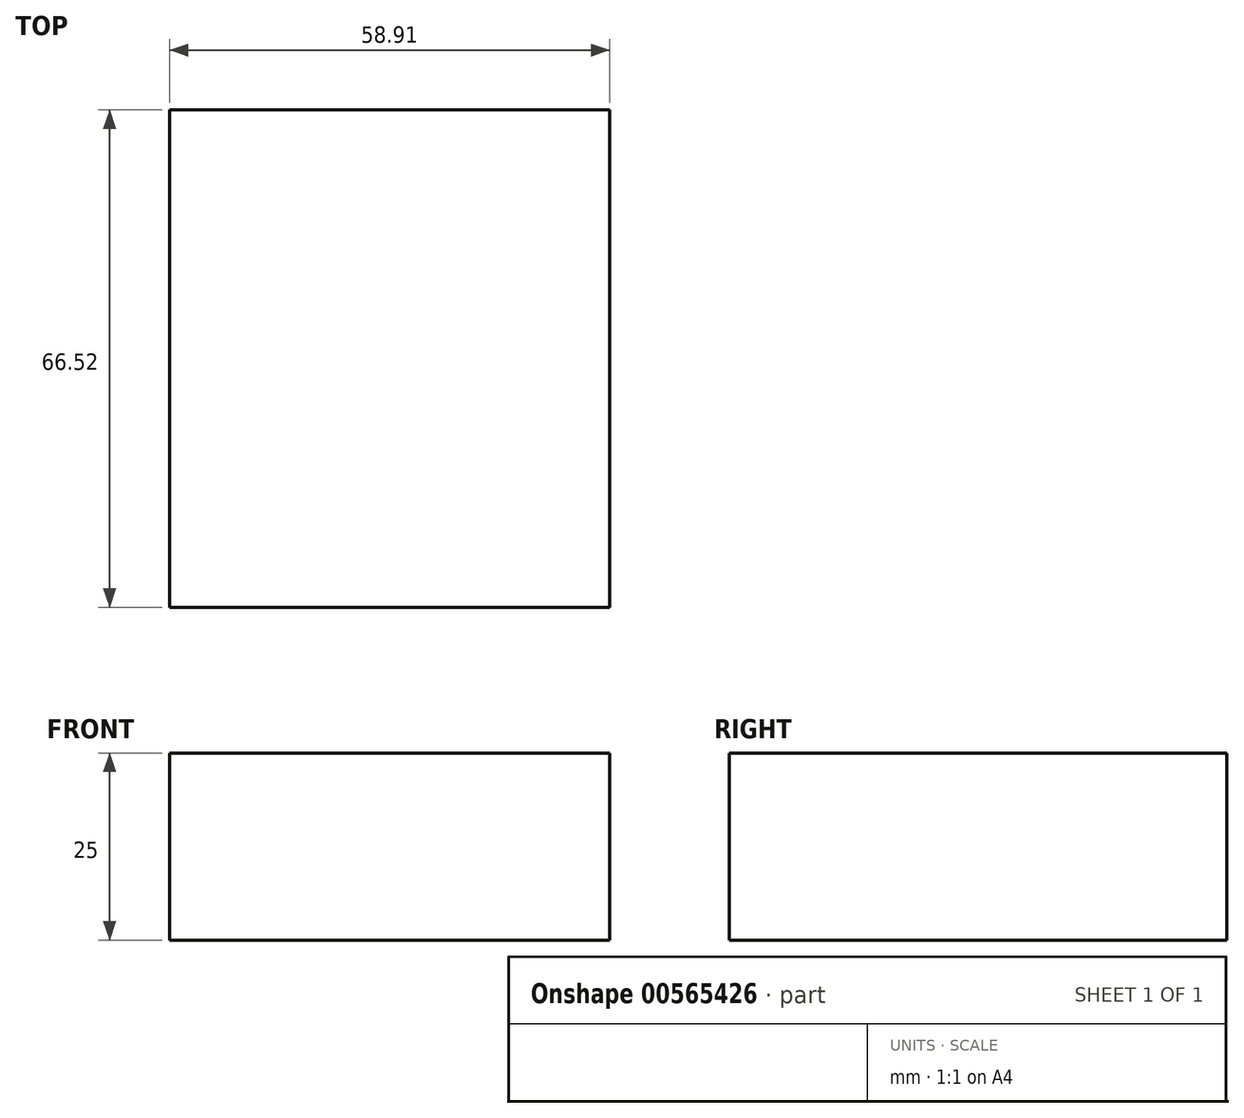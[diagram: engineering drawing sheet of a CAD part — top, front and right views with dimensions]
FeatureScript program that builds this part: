
annotation { "Feature Type Name" : "Feature", "Feature Type Description" : "" }
export const myFeature = defineFeature(function(context is Context, id is Id, definition is map)
    precondition{}
    {
        {
            var Q0;
            Q0=qCreatedBy(makeId("Top.planeOp"),FACE);
            var sketch = newSketch(context, id + "F0", { "sketchPlane" : qUnion([Q0])});
            skLineSegment(sketch, "E0", {"start": v(0, 0) * mm, "end": v(58.91, 0) * mm});
            skLineSegment(sketch, "E1", {"start": v(58.91, 0) * mm, "end": v(58.91, 66.52) * mm});
            skLineSegment(sketch, "E2", {"start": v(58.91, 66.52) * mm, "end": v(0, 66.52) * mm});
            skLineSegment(sketch, "E3", {"start": v(0, 66.52) * mm, "end": v(0, 0) * mm});
            skSolve(sketch);
        }
        {
            var Q0;
            Q0=makeQuery(id+"F0.imprint","IMPRINT",FACE,{"disambiguationData":[TD([[makeQuery(id+"F0.imprint","IMPRINT",EDGE,{"derivedFrom":sQuery(id+"F0.wireOp",EDGE,"E0")}),1.0]])]});
            extrude(context, id + "F1", {"entities" : qUnion([Q0]), "depth" : 25 * mm, "offsetDistance" : 25 * mm});
        }
    });
